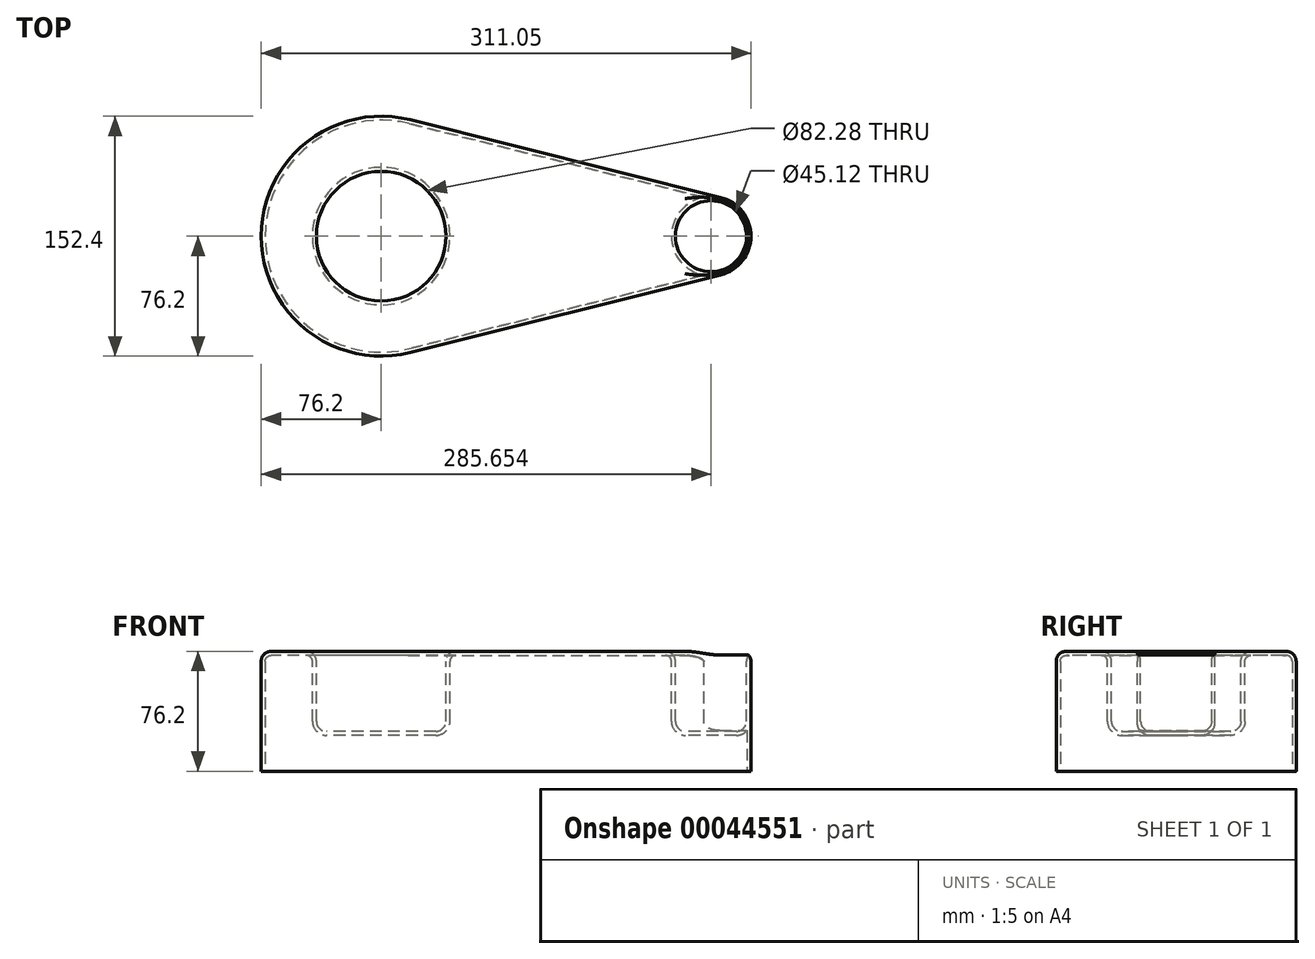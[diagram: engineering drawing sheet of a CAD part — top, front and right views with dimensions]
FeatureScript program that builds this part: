
annotation { "Feature Type Name" : "Feature", "Feature Type Description" : "" }
export const myFeature = defineFeature(function(context is Context, id is Id, definition is map)
    precondition{}
    {
        {
            var Q0;
            Q0=qCreatedBy(makeId("Top.planeOp"),FACE);
            var sketch = newSketch(context, id + "F0", { "sketchPlane" : qUnion([Q0])});
            skCircle(sketch, "E0", {"center": v(0, 0) * mm, "radius": 76.2 * mm});
            skCircle(sketch, "E1", {"center": v(209.45, 0) * mm, "radius": 25.4 * mm});
            skLineSegment(sketch, "E2", {"start": v(18.48, 73.92) * mm, "end": v(215.61, 24.64) * mm});
            skLineSegment(sketch, "E3", {"start": v(18.48, -73.92) * mm, "end": v(215.61, -24.64) * mm});
            skSolve(sketch);
        }
        {
            var Q0;
            {var subQ0=sQuery(id+"F0.wireOp",EDGE,"E2");Q0=makeQuery(id+"F0.imprint","IMPRINT",FACE,{"disambiguationData":[TD([[makeQuery(id+"F0.imprint","IMPRINT",EDGE,{"derivedFrom":subQ0}),-1.0]])]});}
            var Q1;
            {var subQ0=sQuery(id+"F0.wireOp",EDGE,"E0");var subQ2=makeQuery(id+"F0.imprint","INTERSECT",VERTEX,{"derivedFrom":[subQ0,sQuery(id+"F0.wireOp",EDGE,"E2")]});Q1=makeQuery(id+"F0.imprint","IMPRINT",FACE,{"disambiguationData":[TD([[makeQuery(id+"F0.imprint","IMPRINT",EDGE,{"disambiguationData":[TD([[subQ2,-1.0]])],"derivedFrom":subQ0}),1.0]])]});}
            var Q2;
            {var subQ0=sQuery(id+"F0.wireOp",EDGE,"E1");var subQ2=makeQuery(id+"F0.imprint","INTERSECT",VERTEX,{"derivedFrom":[subQ0,sQuery(id+"F0.wireOp",EDGE,"E2")]});Q2=makeQuery(id+"F0.imprint","IMPRINT",FACE,{"disambiguationData":[TD([[makeQuery(id+"F0.imprint","IMPRINT",EDGE,{"disambiguationData":[TD([[subQ2,-1.0]])],"derivedFrom":subQ0}),1.0]])]});}
            extrude(context, id + "F1", {"entities" : qUnion([Q0, Q1, Q2]), "depth" : 76.2 * mm});
        }
        {
            var Q0;
            Q0=makeQuery(id+"F1.opExtrude","CAP_FACE",FACE,{"disambiguationData":[OSD([sQuery(id+"F0.wireOp",EDGE,"E0"),sQuery(id+"F0.wireOp",EDGE,"E1"),sQuery(id+"F0.wireOp",EDGE,"E2"),sQuery(id+"F0.wireOp",EDGE,"E3")])],"isStart":false});
            var sketch = newSketch(context, id + "F2", { "sketchPlane" : qUnion([Q0])});
            skCircle(sketch, "E4", {"center": v(0, 0) * mm, "radius": 41.14 * mm});
            skCircle(sketch, "E5", {"center": v(209.45, 0) * mm, "radius": 22.56 * mm});
            skSolve(sketch);
        }
        {
            var Q0;
            Q0=makeQuery(id+"F2.imprint","IMPRINT",FACE,{"disambiguationData":[TD([[makeQuery(id+"F2.imprint","IMPRINT",EDGE,{"derivedFrom":sQuery(id+"F2.wireOp",EDGE,"E5")}),1.0]])]});
            var Q1;
            Q1=makeQuery(id+"F2.imprint","IMPRINT",FACE,{"disambiguationData":[TD([[makeQuery(id+"F2.imprint","IMPRINT",EDGE,{"derivedFrom":sQuery(id+"F2.wireOp",EDGE,"E4")}),1.0]])]});
            extrude(context, id + "F3", {"entities" : qUnion([Q0, Q1]), "operationType" : NewBodyOperationType.REMOVE, "oppositeDirection" : true, "depth" : 50.8 * mm});
        }
        {
            var Q0;
            Q0=makeQuery(id+"F1.opExtrude","CAP_EDGE",EDGE,{"disambiguationData":[OSD([sQuery(id+"F0.wireOp",EDGE,"E3")])],"isStart":false});
            var Q1;
            Q1=makeQuery(id+"F1.opExtrude","CAP_FACE",FACE,{"disambiguationData":[OSD([sQuery(id+"F0.wireOp",EDGE,"E0"),sQuery(id+"F0.wireOp",EDGE,"E1"),sQuery(id+"F0.wireOp",EDGE,"E2"),sQuery(id+"F0.wireOp",EDGE,"E3")])],"isStart":false});
            var Q2;
            Q2=makeQuery(id+"F3.boolean.opBoolean","COPY",FACE,{"derivedFrom":makeQuery(id+"F3.opExtrude","CAP_FACE",FACE,{"disambiguationData":[OSD([sQuery(id+"F2.wireOp",EDGE,"E4")])],"isStart":false})});
            var Q3;
            Q3=makeQuery(id+"F3.boolean.opBoolean","COPY",EDGE,{"derivedFrom":makeQuery(id+"F3.opExtrude","CAP_EDGE",EDGE,{"disambiguationData":[OSD([sQuery(id+"F2.wireOp",EDGE,"E5")])],"isStart":false})});
            fillet(context, id + "F4", {"entities" : qUnion([Q0, Q1, Q2, Q3]), "radius" : 6.35 * mm, "tangentPropagation" : true, "allowEdgeOverflow" : false});
        }
        {
            var Q0;
            Q0=makeQuery(id+"F1.opExtrude","CAP_FACE",FACE,{"disambiguationData":[OSD([sQuery(id+"F0.wireOp",EDGE,"E0"),sQuery(id+"F0.wireOp",EDGE,"E1"),sQuery(id+"F0.wireOp",EDGE,"E2"),sQuery(id+"F0.wireOp",EDGE,"E3")])],"isStart":true});
            shell(context, id + "F5", {"entities" : qUnion([Q0]), "thickness" : 2.54 * mm});
        }
    });
